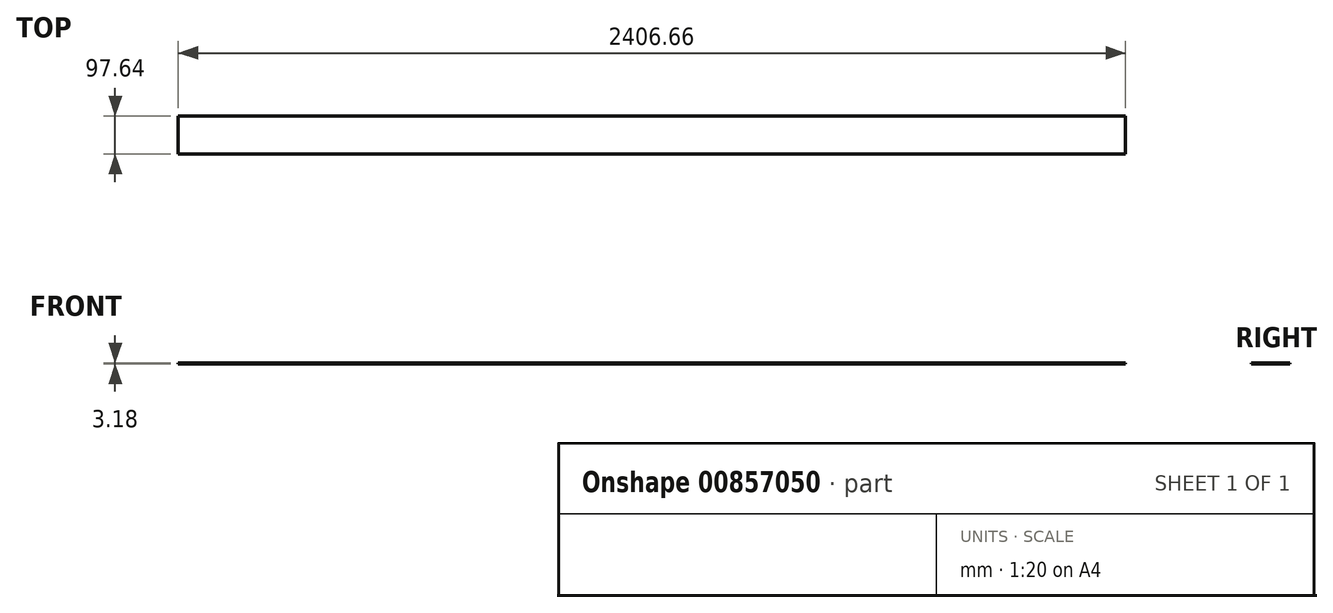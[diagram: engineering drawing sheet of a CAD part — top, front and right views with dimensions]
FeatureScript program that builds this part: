
annotation { "Feature Type Name" : "Feature", "Feature Type Description" : "" }
export const myFeature = defineFeature(function(context is Context, id is Id, definition is map)
    precondition{}
    {
        {
            var Q0;
            Q0=qCreatedBy(makeId("Right.planeOp"),FACE);
            var sketch = newSketch(context, id + "F0", { "sketchPlane" : qUnion([Q0])});
            skLineSegment(sketch, "E0.bottom", {"start": v(-48.82, 1.59) * mm, "end": v(48.82, 1.59) * mm});
            skLineSegment(sketch, "E0.top", {"start": v(-48.82, -1.59) * mm, "end": v(48.82, -1.59) * mm});
            skLineSegment(sketch, "E0.left", {"start": v(-48.82, 1.59) * mm, "end": v(-48.82, -1.59) * mm});
            skLineSegment(sketch, "E0.right", {"start": v(48.82, 1.59) * mm, "end": v(48.82, -1.59) * mm});
            skPoint(sketch, "E0.middle", {"position": v(0, 0) * mm});
            skSolve(sketch);
        }
        {
            var Q0;
            Q0 = qSketchRegion(id + "F0", true);
            extrude(context, id + "F1", {"entities" : qUnion([Q0]), "depth" : 2406.65 * mm, "offsetDistance" : 25.4 * mm, "symmetric" : true});
        }
        {
            var Q0;
            Q0=makeQuery(id+"F1.opExtrude","SWEPT_FACE",FACE,{"disambiguationData":[OSD([sQuery(id+"F0.wireOp",EDGE,"E0.right")])]});
            var sketch = newSketch(context, id + "F2", { "sketchPlane" : qUnion([Q0])});
            skLineSegment(sketch, "E1.bottom", {"start": v(-22.23, 1.59) * mm, "end": v(22.23, 1.59) * mm});
            skLineSegment(sketch, "E1.top", {"start": v(-22.23, -1.59) * mm, "end": v(22.23, -1.59) * mm});
            skLineSegment(sketch, "E1.left", {"start": v(-22.23, 1.59) * mm, "end": v(-22.23, -1.59) * mm});
            skLineSegment(sketch, "E1.right", {"start": v(22.23, 1.59) * mm, "end": v(22.23, -1.59) * mm});
            skPoint(sketch, "E1.middle", {"position": v(0, 0) * mm});
            skSolve(sketch);
        }
    });
